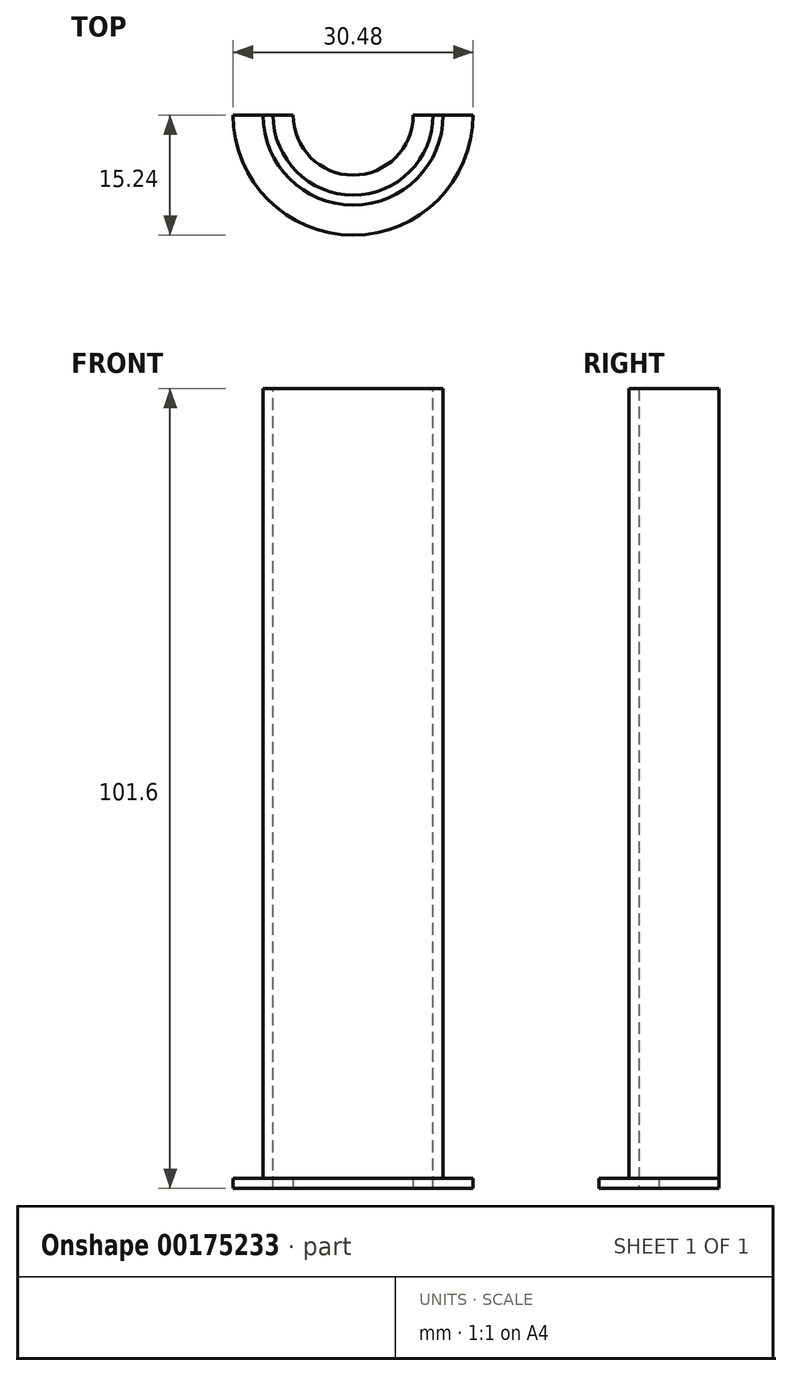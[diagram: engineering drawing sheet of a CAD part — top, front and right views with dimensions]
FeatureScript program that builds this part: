
annotation { "Feature Type Name" : "Feature", "Feature Type Description" : "" }
export const myFeature = defineFeature(function(context is Context, id is Id, definition is map)
    precondition{}
    {
        {
            var Q0;
            Q0=qCreatedBy(makeId("Front.planeOp"),FACE);
            var sketch = newSketch(context, id + "F0", { "sketchPlane" : qUnion([Q0])});
            skLineSegment(sketch, "E0.bottom", {"start": v(0, 0) * mm, "end": v(1.27, 0) * mm});
            skLineSegment(sketch, "E0.top", {"start": v(0, 101.6) * mm, "end": v(1.27, 101.6) * mm});
            skLineSegment(sketch, "E0.left", {"start": v(0, 0) * mm, "end": v(0, 101.6) * mm});
            skLineSegment(sketch, "E0.right", {"start": v(1.27, 0) * mm, "end": v(1.27, 101.6) * mm});
            skLineSegment(sketch, "E1.bottom", {"start": v(0, 0) * mm, "end": v(-3.81, 0) * mm});
            skLineSegment(sketch, "E1.top", {"start": v(0, 1.27) * mm, "end": v(-3.81, 1.27) * mm});
            skLineSegment(sketch, "E1.left", {"start": v(0, 0) * mm, "end": v(0, 1.27) * mm});
            skLineSegment(sketch, "E1.right", {"start": v(-3.8, 0) * mm, "end": v(-3.81, 1.27) * mm});
            skLineSegment(sketch, "E2", {"start": v(11.43, 0) * mm, "end": v(11.43, 101.6) * mm});
            skSolve(sketch);
        }
        {
            var Q0;
            Q0=makeQuery(id+"F0.imprint","IMPRINT",FACE,{"disambiguationData":[TD([[makeQuery(id+"F0.imprint","IMPRINT",EDGE,{"derivedFrom":sQuery(id+"F0.wireOp",EDGE,"E1.bottom")}),-1.0]])]});
            var Q1;
            Q1=makeQuery(id+"F0.imprint","IMPRINT",FACE,{"disambiguationData":[TD([[makeQuery(id+"F0.imprint","IMPRINT",EDGE,{"derivedFrom":sQuery(id+"F0.wireOp",EDGE,"E0.bottom")}),1.0]])]});
            var Q2;
            Q2=sQuery(id+"F0.wireOp",EDGE,"E2");
            revolve(context, id + "F1", {"entities" : qUnion([Q0, Q1]), "axis" : qUnion([Q2]), "revolveType" : RevolveType.ONE_DIRECTION, "angle" : 180 * degree});
        }
        {
            var Q0;
            Q0 = qSketchRegion(id + "F0", true);
            var Q1;
            Q1=sQuery(id+"F0.wireOp",EDGE,"E2");
            revolve(context, id + "F2", {"entities" : qUnion([Q0]), "axis" : qUnion([Q1]), "revolveType" : RevolveType.ONE_DIRECTION, "angle" : 180 * degree});
        }
        {
            var Q0;
            Q0=makeQuery(id+"F1.opRevolve","SWEPT_FACE",FACE,{"disambiguationData":[OSD([sQuery(id+"F0.wireOp",EDGE,"E0.bottom"),sQuery(id+"F0.wireOp",EDGE,"E1.bottom")])]});
            var sketch = newSketch(context, id + "F3", { "sketchPlane" : qUnion([Q0])});
            skCircle(sketch, "E3", {"center": v(11.43, 0) * mm, "radius": 7.62 * mm});
            skLineSegment(sketch, "E4", {"start": v(-3.81, 0) * mm, "end": v(26.67, 0) * mm});
            skSolve(sketch);
        }
        {
            var Q0;
            {var subQ4=makeQuery(id+"F1.opRevolve","SWEPT_EDGE",EDGE,{"disambiguationData":[OSD([sQuery(id+"F0.wireOp",EDGE,"E0.bottom"),sQuery(id+"F0.wireOp",EDGE,"E0.right")])]});Q0=makeQuery(id+"F3.imprint","IMPRINT",FACE,{"disambiguationData":[TD([[makeQuery(id+"F3.imprint","IMPRINT",EDGE,{"derivedFrom":subQ4}),-1.0]])]});}
            var Q1;
            {var subQ1=makeQuery(id+"F1.opRevolve","SWEPT_EDGE",EDGE,{"disambiguationData":[OSD([sQuery(id+"F0.wireOp",EDGE,"E0.bottom"),sQuery(id+"F0.wireOp",EDGE,"E0.right")])]});Q1=makeQuery(id+"F3.imprint","IMPRINT",FACE,{"disambiguationData":[TD([[makeQuery(id+"F3.imprint","IMPRINT",EDGE,{"derivedFrom":subQ1}),1.0]])]});}
            extrude(context, id + "F4", {"entities" : qUnion([Q0, Q1]), "oppositeDirection" : true, "depth" : 1.27 * mm});
        }
    });
